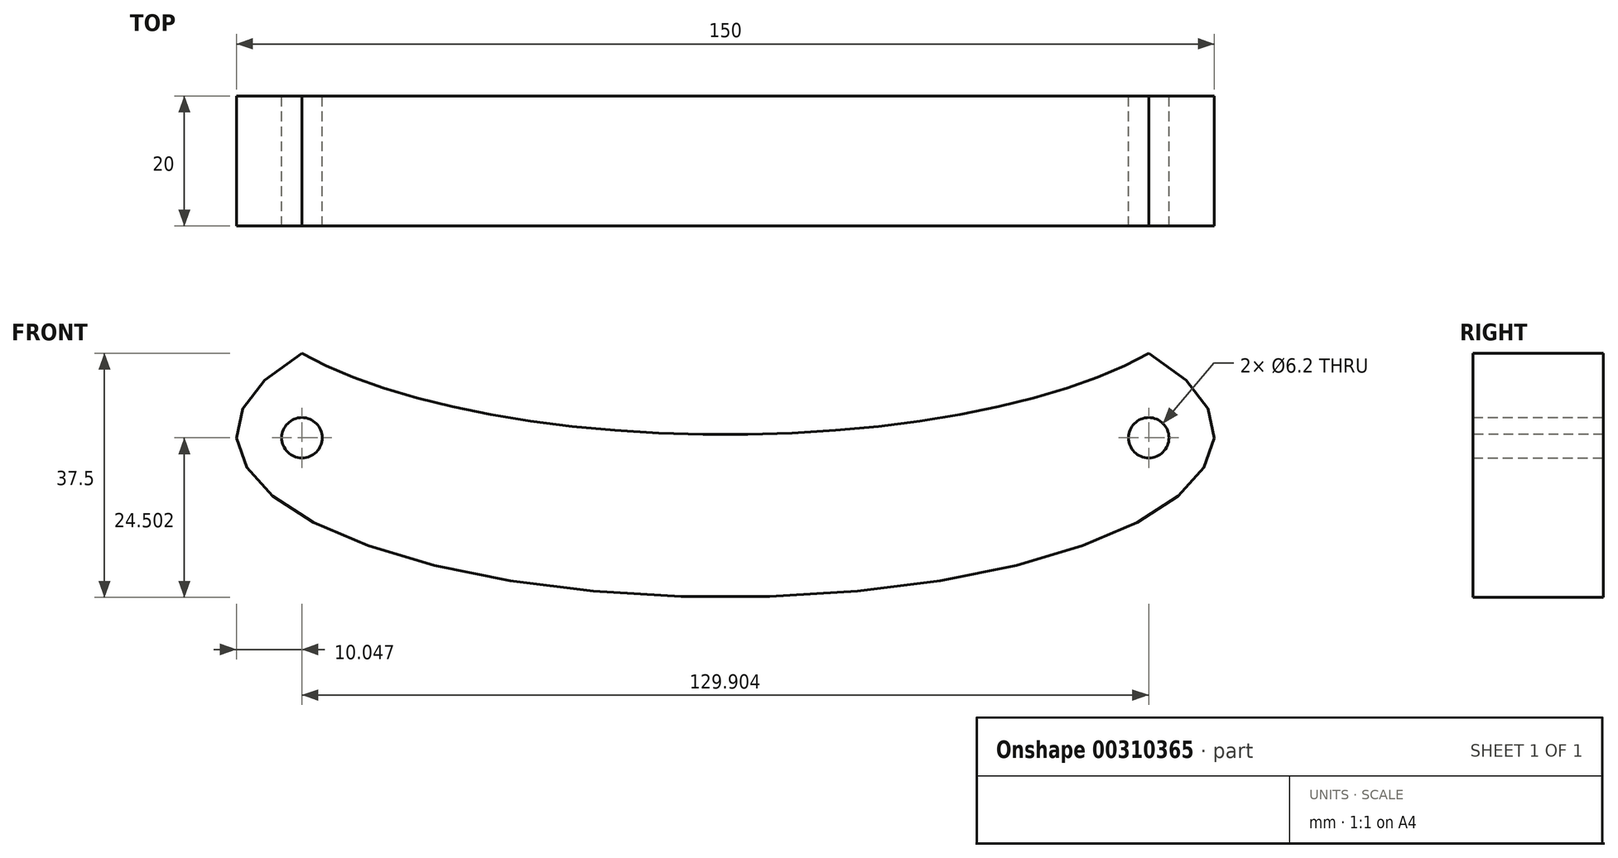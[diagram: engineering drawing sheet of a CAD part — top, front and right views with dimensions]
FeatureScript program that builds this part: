
annotation { "Feature Type Name" : "Feature", "Feature Type Description" : "" }
export const myFeature = defineFeature(function(context is Context, id is Id, definition is map)
    precondition{}
    {
        {
            var Q0;
            Q0=qCreatedBy(makeId("Front.planeOp"),FACE);
            var sketch = newSketch(context, id + "F0", { "sketchPlane" : qUnion([Q0])});
            skEllipticalArc(sketch, "E0", {});
            skEllipticalArc(sketch, "E1", {});
            skCircle(sketch, "E2", {"center": v(-70.97, 1.85) * mm, "radius": 3.1 * mm});
            skCircle(sketch, "E3", {"center": v(58.93, 1.85) * mm, "radius": 3.1 * mm});
            const initialGuessF0  = {"E0": [-0.0060215056873857975, 0.002352150622755289, 1, 0, 0.075, 0.025, 2.617993877991495, 0.5235987755982993], "E1": [-0.006021505687385793, 0.02735215062275529, 1, 0, 0.075, 0.025, 3.6651914291880914, 5.759586531581287]};
            skSetInitialGuess(sketch, initialGuessF0);
            skSolve(sketch);
        }
        {
            var Q0;
            Q0 = qSketchRegion(id + "F0", true);
            extrude(context, id + "F1", {"entities" : qUnion([Q0]), "depth" : 20 * mm});
        }
    });
